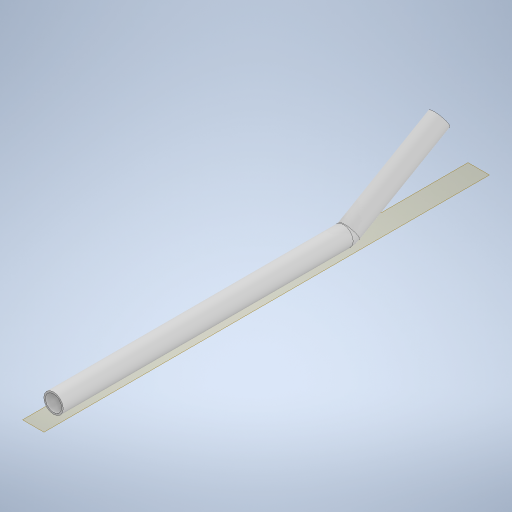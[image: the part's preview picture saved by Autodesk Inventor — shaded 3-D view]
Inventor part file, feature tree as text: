
AUTODESK INVENTOR PART (.ipt)
format: ipt  version: 2024 (Build 280153000, 153)  size: 252,928 bytes
history: native  units: in
note: dims shown in document units (in); Inventor stores cm internally (conversion verified against a paired STEP export)
features: sketch x2, extrude x1, plane x1, other x1
ambient origin geometry x8: Origin, YZ Plane, XZ Plane, XY Plane, X Axis, Y Axis, Z Axis, Center Point
bodies: Solid1 (feature_tree)
feature tree (5):
  extrude  "Extrusion1"  Depth=0.7874in
  plane  "Work Plane1"
  other  "Bend Part1"
  sketch  "Sketch1"  dims[d0=0.9449in d1=0.7874in]
  sketch  "Sketch2"  dims[d2=19.685in d3=0.0in d4=5.5906in d5=1.0in d6=30.0deg]
